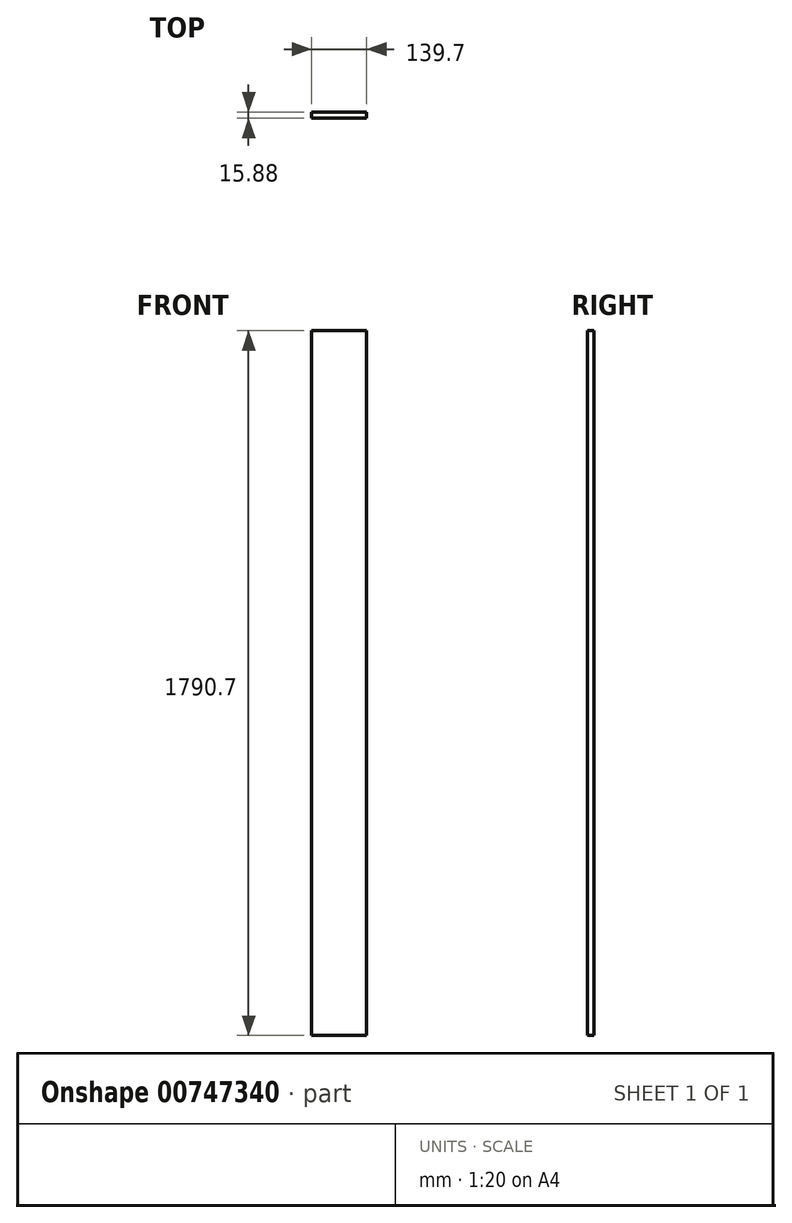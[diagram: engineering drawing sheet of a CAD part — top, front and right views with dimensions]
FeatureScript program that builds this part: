
annotation { "Feature Type Name" : "Feature", "Feature Type Description" : "" }
export const myFeature = defineFeature(function(context is Context, id is Id, definition is map)
    precondition{}
    {
        {
            var Q0;
            Q0=qCreatedBy(makeId("Front.planeOp"),FACE);
            var sketch = newSketch(context, id + "F0", { "sketchPlane" : qUnion([Q0])});
            skLineSegment(sketch, "E0.bottom", {"start": v(0, 0) * mm, "end": v(139.7, 0) * mm});
            skLineSegment(sketch, "E0.top", {"start": v(0, 1790.7) * mm, "end": v(139.7, 1790.7) * mm});
            skLineSegment(sketch, "E0.left", {"start": v(0, 0) * mm, "end": v(0, 1790.7) * mm});
            skLineSegment(sketch, "E0.right", {"start": v(139.7, 0) * mm, "end": v(139.7, 1790.7) * mm});
            skSolve(sketch);
        }
        {
            var Q0;
            Q0=makeQuery(id+"F0.imprint","IMPRINT",FACE,{"disambiguationData":[TD([[makeQuery(id+"F0.imprint","IMPRINT",EDGE,{"derivedFrom":sQuery(id+"F0.wireOp",EDGE,"E0.bottom")}),1.0]])]});
            extrude(context, id + "F1", {"entities" : qUnion([Q0]), "depth" : 15.88 * mm, "offsetDistance" : 25.4 * mm});
        }
    });
